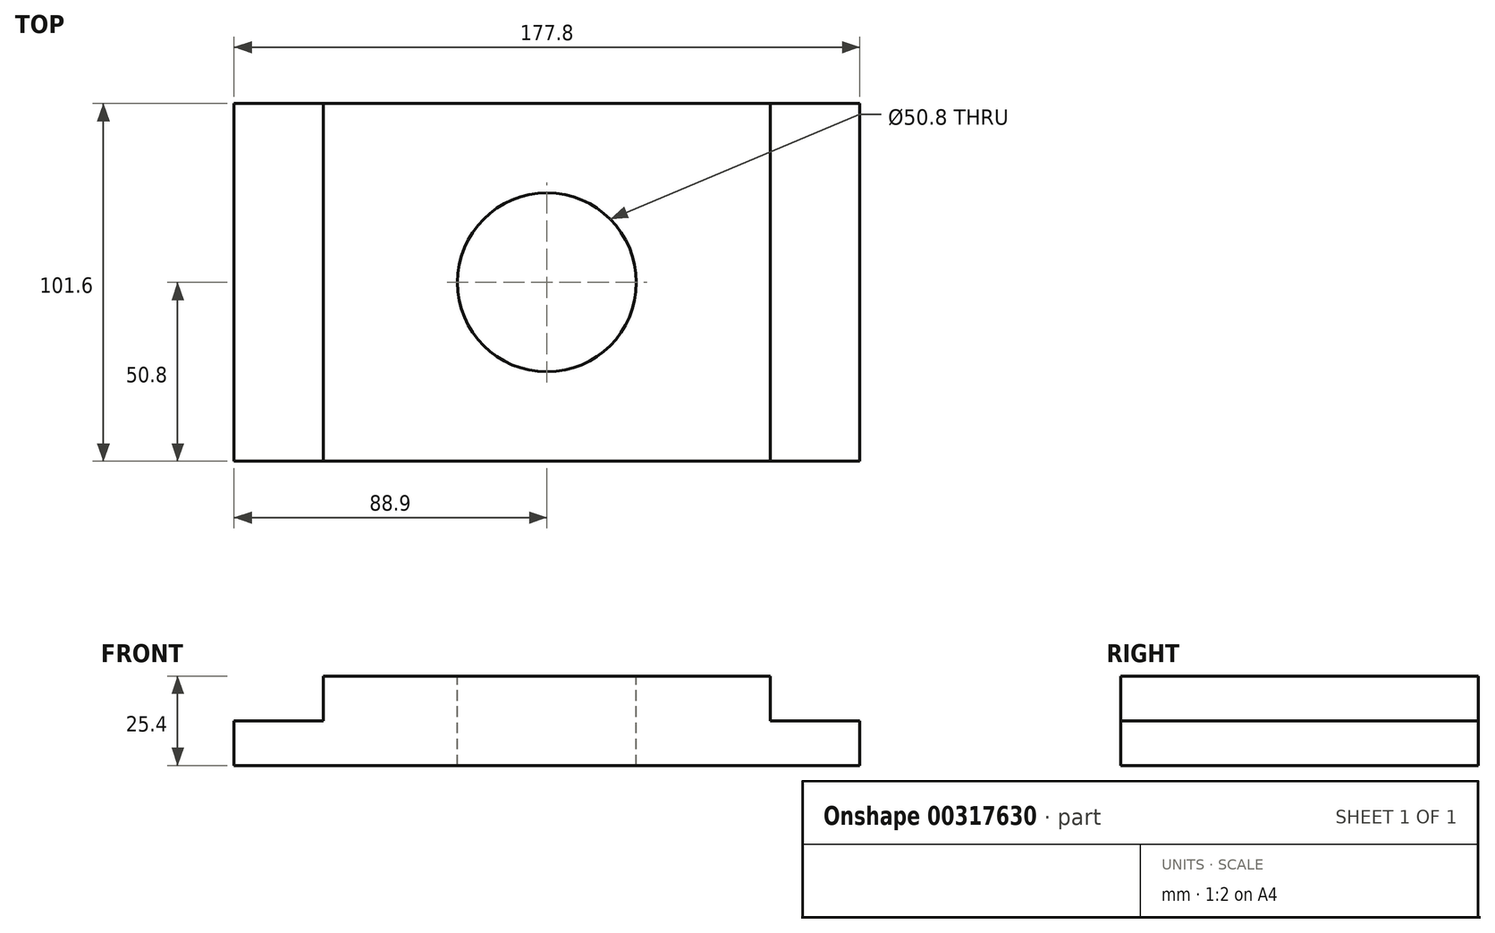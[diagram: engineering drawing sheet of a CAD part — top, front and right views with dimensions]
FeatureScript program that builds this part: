
annotation { "Feature Type Name" : "Feature", "Feature Type Description" : "" }
export const myFeature = defineFeature(function(context is Context, id is Id, definition is map)
    precondition{}
    {
        {
            var Q0;
            Q0=qCreatedBy(makeId("Front.planeOp"),FACE);
            var sketch = newSketch(context, id + "F0", { "sketchPlane" : qUnion([Q0])});
            skLineSegment(sketch, "E0.bottom", {"start": v(0, 0) * mm, "end": v(177.8, 0) * mm});
            skLineSegment(sketch, "E0.top", {"start": v(0, 25.4) * mm, "end": v(177.8, 25.4) * mm});
            skLineSegment(sketch, "E0.left", {"start": v(0, 0) * mm, "end": v(0, 25.4) * mm});
            skLineSegment(sketch, "E0.right", {"start": v(177.8, 0) * mm, "end": v(177.8, 25.4) * mm});
            skSolve(sketch);
        }
        {
            var Q0;
            Q0=makeQuery(id+"F0.imprint","IMPRINT",FACE,{"disambiguationData":[TD([[makeQuery(id+"F0.imprint","IMPRINT",EDGE,{"derivedFrom":sQuery(id+"F0.wireOp",EDGE,"E0.bottom")}),1.0]])]});
            extrude(context, id + "F1", {"entities" : qUnion([Q0]), "depth" : 101.6 * mm});
        }
        {
            var Q0;
            Q0=makeQuery(id+"F1.opExtrude","SWEPT_FACE",FACE,{"disambiguationData":[OSD([sQuery(id+"F0.wireOp",EDGE,"E0.top")])]});
            var sketch = newSketch(context, id + "F2", { "sketchPlane" : qUnion([Q0])});
            skCircle(sketch, "E1", {"center": v(88.9, -50.8) * mm, "radius": 25.4 * mm});
            skLineSegment(sketch, "E2", {"start": v(0, 0) * mm, "end": v(177.8, -101.6) * mm, "construction": true});
            skSolve(sketch);
        }
        {
            var Q0;
            Q0=makeQuery(id+"F2.imprint","IMPRINT",FACE,{"disambiguationData":[TD([[makeQuery(id+"F2.imprint","IMPRINT",EDGE,{"derivedFrom":sQuery(id+"F2.wireOp",EDGE,"E1")}),1.0]])]});
            extrude(context, id + "F3", {"entities" : qUnion([Q0]), "operationType" : NewBodyOperationType.REMOVE, "endBound" : BoundingType.THROUGH_ALL, "oppositeDirection" : true, "depth" : 25.4 * mm});
        }
        {
            var Q0;
            Q0=makeQuery(id+"F1.opExtrude","CAP_FACE",FACE,{"disambiguationData":[OSD([sQuery(id+"F0.wireOp",EDGE,"E0.bottom"),sQuery(id+"F0.wireOp",EDGE,"E0.top"),sQuery(id+"F0.wireOp",EDGE,"E0.left"),sQuery(id+"F0.wireOp",EDGE,"E0.right")])],"isStart":false});
            var sketch = newSketch(context, id + "F4", { "sketchPlane" : qUnion([Q0])});
            skLineSegment(sketch, "E3.bottom", {"start": v(0, 25.4) * mm, "end": v(25.4, 25.4) * mm});
            skLineSegment(sketch, "E3.top", {"start": v(0, 12.7) * mm, "end": v(25.4, 12.7) * mm});
            skLineSegment(sketch, "E3.left", {"start": v(0, 25.4) * mm, "end": v(0, 12.7) * mm});
            skLineSegment(sketch, "E3.right", {"start": v(25.4, 25.4) * mm, "end": v(25.4, 12.7) * mm});
            skLineSegment(sketch, "E4.bottom", {"start": v(177.8, 25.4) * mm, "end": v(152.4, 25.4) * mm});
            skLineSegment(sketch, "E4.top", {"start": v(177.8, 12.7) * mm, "end": v(152.4, 12.7) * mm});
            skLineSegment(sketch, "E4.left", {"start": v(177.8, 25.4) * mm, "end": v(177.8, 12.7) * mm});
            skLineSegment(sketch, "E4.right", {"start": v(152.4, 25.4) * mm, "end": v(152.4, 12.7) * mm});
            skSolve(sketch);
        }
        {
            var Q0;
            Q0=makeQuery(id+"F4.imprint","IMPRINT",FACE,{"disambiguationData":[TD([[makeQuery(id+"F4.imprint","IMPRINT",EDGE,{"derivedFrom":sQuery(id+"F4.wireOp",EDGE,"E3.bottom")}),-1.0]])]});
            var Q1;
            Q1=makeQuery(id+"F4.imprint","IMPRINT",FACE,{"disambiguationData":[TD([[makeQuery(id+"F4.imprint","IMPRINT",EDGE,{"derivedFrom":sQuery(id+"F4.wireOp",EDGE,"E4.bottom")}),-1.0]])]});
            extrude(context, id + "F5", {"entities" : qUnion([Q0, Q1]), "operationType" : NewBodyOperationType.REMOVE, "endBound" : BoundingType.THROUGH_ALL, "oppositeDirection" : true, "depth" : 25.4 * mm});
        }
    });
